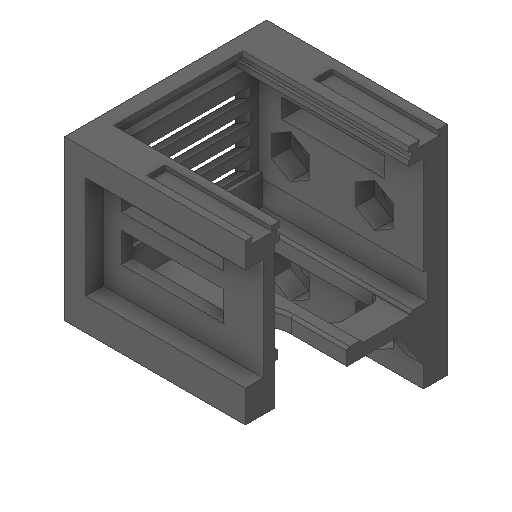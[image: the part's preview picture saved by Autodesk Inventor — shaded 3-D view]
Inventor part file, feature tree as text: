
AUTODESK INVENTOR PART (.ipt)
format: ipt  version: 2022 (Build 260153000, 153)  size: 778,752 bytes
history: native  units: mm
features: sketch x35, extrude x34, projected_geometry x28, chamfer x6, thicken_offset x3, plane x3, fillet x1, other x1, sweep x1
ambient origin geometry x8: Origin, YZ Plane, XZ Plane, XY Plane, X Axis, Y Axis, Z Axis, Center Point
bodies: Solid1 (feature_tree)
feature tree (112):
  extrude  "Extrusion1"  Depth=31.267mm
  extrude  "Extrusion2"  Depth=6.26mm TaperAngle=0.0deg
  extrude  "Extrusion3"  Depth=0.7mm
  extrude  "Extrusion4"  Depth=1.0mm TaperAngle=0.0deg
  extrude  "Extrusion5"  Depth=24.0mm TaperAngle=0.0deg
  extrude  "Extrusion6"  Depth=2.815mm
  extrude  "Extrusion7"  Depth=0.575mm
  extrude  "Extrusion8"  Depth=0.575mm
  extrude  "Extrusion9"  Depth=2.0mm
  extrude  "Extrusion10"  Depth=3.0mm TaperAngle=0.0deg
  sketch  "Sketch13"  dims[d30=9.07mm d31=22.25mm d32=1.66mm]
  extrude  "Extrusion11"  Depth=1.66mm
  fillet  "Fillet1"  Radius=1.66mm
  extrude  "Extrusion14"  Depth=3.245mm
  thicken_offset  "Thicken1"
  other  "available_for_screw"
  thicken_offset  "Thicken2"
  sketch  "Sketch20"  dims[d35=3.505mm d36=20.695mm]
  extrude  "Extrusion17"  Depth=3.505mm
  extrude  "Extrusion18"  Depth=3.0mm TaperAngle=0.0deg
  thicken_offset  "Thicken4"
  extrude  "Extrusion19"  Depth=10.0mm TaperAngle=0.0deg
  extrude  "Extrusion20"  Depth=0.5mm
  extrude  "Extrusion21"  Depth=0.315mm
  extrude  "Extrusion22"  Depth=0.1mm
  sweep  "Sweep1"
  extrude  "Extrusion23"  Depth=3.602mm
  chamfer  "Chamfer2"  Distance=33.125mm
  extrude  "Extrusion24"  Depth=11.2mm
  sketch  "Sketch30"  dims[d67=7.4mm d69=33.125mm d70=0.0mm]
  plane  "Work Plane1"
  extrude  "Extrusion25"  Depth=1.0mm
  extrude  "Extrusion43"  Depth=1.0mm
  extrude  "Extrusion26"  Depth=7.12mm
  extrude  "Extrusion28"  Depth=4.5mm
  extrude  "Extrusion34"  Depth=16.0mm
  extrude  "Extrusion35"  Depth=3.175mm TaperAngle=0.0deg
  extrude  "Extrusion36"  Depth=0.7mm
  sketch  "Sketch42"  dims[d105=7.12mm]
  extrude  "Extrusion40"  Depth=11.0mm
  chamfer  "Chamfer3"  Distance=7.12mm
  chamfer  "Chamfer4"  Distance=3.5mm
  chamfer  "Chamfer5"  Distance=3.5mm
  chamfer  "Chamfer6"  Distance=5.0mm
  chamfer  "Chamfer7"  Distance=3.0mm
  extrude  "Extrusion41"  Depth=3.0mm TaperAngle=0.0deg
  extrude  "Extrusion42"  Depth=8.0mm
  plane  "Work Plane2"
  extrude  "Extrusion30"  Depth=2.0mm
  plane  "Work Plane3"
  extrude  "Extrusion31"  Depth=6.0mm
  extrude  "Extrusion33"  Depth=6.0mm
  extrude  "Extrusion32"  Depth=4.0mm
  sketch  "Sketch1"  dims[d0=29.05mm d1=31.267mm]
  sketch  "Sketch2"  dims[d2=3.0mm d3=6.26mm d4=0.0mm]
  projected_geometry  "Projected Loop1"
  sketch  "Sketch3"  dims[d5=0.7mm d6=0.7mm]
  projected_geometry  "Projected Loop2"
  sketch  "Sketch4"  dims[d7=0.7mm d8=1.0mm d9=0.0mm]
  projected_geometry  "Projected Loop3"
  sketch  "Sketch7"  dims[d10=0.5mm d11=0.0mm d12=24.0mm d13=0.0mm]
  sketch  "Sketch8"  dims[d15=2.385mm d17=2.815mm]
  projected_geometry  "Projected Loop4"
  sketch  "Sketch9"  dims[d18=1.0mm d19=0.0mm d20=0.575mm]
  projected_geometry  "Projected Loop5"
  sketch  "Sketch10"  dims[d21=0.5mm d22=0.575mm]
  sketch  "Sketch11"  dims[d23=1.25mm d24=0.0mm d25=2.0mm]
  sketch  "Sketch12"  dims[d26=1.0mm d27=0.0mm d28=3.0mm d29=0.0mm]
  projected_geometry  "Projected Loop6"
  projected_geometry  "Projected Loop7"
  projected_geometry  "Projected Loop8"
  sketch  "Sketch16"  dims[d33=13.67mm d34=3.245mm]
  projected_geometry  "Projected Loop9"
  sketch  "Sketch21"  dims[d37=6.975mm d38=3.0mm d39=0.0mm]
  projected_geometry  "Projected Loop12"
  projected_geometry  "Projected Loop13"
  sketch  "Sketch22"  dims[d40=0.6mm d41=10.0mm d42=0.0mm]
  sketch  "Sketch24"  dims[d43=10.0mm d44=0.0mm d45=0.5mm]
  sketch  "Sketch25"  dims[d58=0.315mm d59=19.79mm]
  projected_geometry  "Projected Loop15"
  sketch  "Sketch26"  dims[d60=0.1mm d61=3.175mm]
  projected_geometry  "Projected Loop16"
  projected_geometry  "Projected Loop17"
  sketch  "Sketch27"  dims[d62=0.1mm d63=7.4mm]
  sketch  "Sketch28"  dims[d64=19.25mm d65=3.602mm]
  projected_geometry  "Projected Loop18"
  sketch  "Sketch29"  dims[d66=19.4405mm]
  projected_geometry  "Projected Loop19"
  sketch  "Sketch31"  dims[d71=2.475mm d72=1.175mm d82=11.2mm]
  projected_geometry  "Projected Loop20"
  sketch  "Sketch32"  dims[d83=0.1mm d84=1.0mm]
  sketch  "Sketch34"  dims[d85=1.0mm d86=0.8mm d87=1.0mm]
  projected_geometry  "Projected Loop22"
  sketch  "Sketch35"  dims[d88=6.0mm d89=7.12mm]
  projected_geometry  "Projected Loop23"
  sketch  "Sketch36"  dims[d90=4.5mm d91=4.08mm]
  projected_geometry  "Projected Loop24"
  projected_geometry  "Projected Loop25"
  sketch  "Sketch37"  dims[d92=7.12mm d94=16.0mm]
  projected_geometry  "Projected Loop26"
  sketch  "Sketch39"  dims[d95=4.08mm d96=3.175mm d97=0.0mm]
  projected_geometry  "Projected Loop28"
  sketch  "Sketch40"  dims[d98=2.8mm d99=0.0mm d102=0.7mm]
  sketch  "Sketch41"  dims[d103=0.7mm d104=11.0mm]
  projected_geometry  "Projected Loop29"
  projected_geometry  "Projected Loop30"
  sketch  "Sketch43"  dims[d106=1.0mm]
  projected_geometry  "Projected Loop31"
  sketch  "Sketch44"  dims[d107=4.08mm]
  sketch  "Sketch45"  dims[d108=4.08mm d109=7.12mm d110=3.5mm d111=0.0mm d112=3.5mm d113=0.0mm d118=5.0mm d120=3.0mm d121=0.0mm d122=3.0mm d123=0.0mm d124=8.0mm d125=2.0mm d126=6.0mm d127=6.0mm d128=40.0mm d130=4.0mm d131=10.0mm d133=10.0mm d135=30.0deg d136=4.0mm d137=0.0mm d138=0.0mm d139=4.0mm d140=19.4405mm d141=2.0mm d142=3.375mm d143=0.0mm d144=4.0mm d145=2.0mm d146=45.0deg d147=3.0mm d149=10.0mm d150=0.0mm d151=2.0mm d152=0.1mm d153=10.0mm d154=0.0mm d155=10.36mm d156=1.5mm d157=0.0mm d158=10.2mm d159=10.1mm d161=1.0mm d162=1.0mm d163=1.0mm d166=12.1mm d167=1.0mm d168=1.0mm d169=1.0mm d170=1.0mm d174=8.0mm d175=0.0mm d178=0.3mm d179=0.3mm d180=0.3mm d181=0.3mm d182=0.5mm d183=0.0mm d184=0.5mm d185=0.0mm d186=45.0deg d187=0.5mm d188=0.4mm d189=0.0mm d190=45.0deg d191=0.5mm d192=0.4mm d193=0.0mm d194=6.34mm d196=5.84mm d197=0.5mm d198=0.0mm d199=1.2mm d200=0.0mm d202=0.5mm d203=0.5mm d204=0.5mm d205=0.5mm d206=1.7mm d207=0.0mm d217=0.3mm d218=0.0mm d219=0.5mm d220=2.0mm d221=45.0deg d222=0.5mm d223=2.0mm d224=45.0deg d225=0.5mm d226=2.0mm d227=45.0deg d228=0.2mm d229=2.0mm d230=45.0deg d231=0.2mm d232=2.0mm d233=45.0deg d234=45.0deg d235=0.5mm d236=0.3mm d237=0.0mm d238=45.0deg d239=0.5mm d240=0.3mm d241=0.0mm d243=1.1mm d244=12.217305mm d245=12.217305mm d246=4.2mm d247=1.0mm d248=4.2mm d249=1.5mm d250=12.217305mm d251=12.217305mm d252=1.1mm d253=20.1mm d254=0.0mm]
  projected_geometry  "Projected Loop32"
  projected_geometry  "Projected Loop33"
